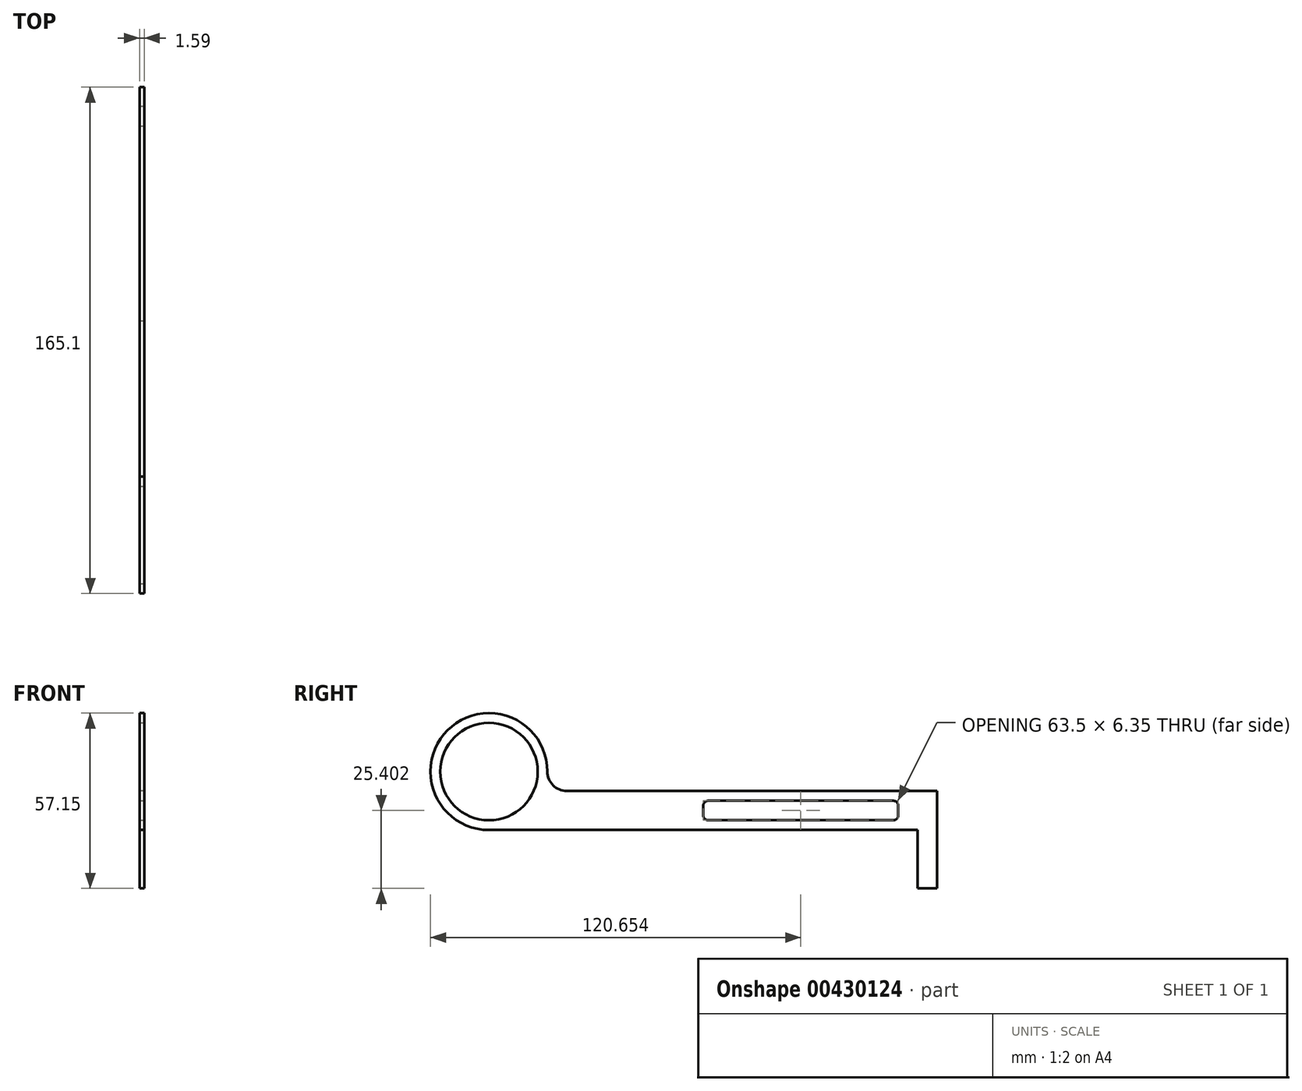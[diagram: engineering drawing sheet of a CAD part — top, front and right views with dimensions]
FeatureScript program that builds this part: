
annotation { "Feature Type Name" : "Feature", "Feature Type Description" : "" }
export const myFeature = defineFeature(function(context is Context, id is Id, definition is map)
    precondition{}
    {
        {
            var Q0;
            Q0=qCreatedBy(makeId("Right.planeOp"),FACE);
            var sketch = newSketch(context, id + "F0", { "sketchPlane" : qUnion([Q0])});
            skLineSegment(sketch, "E0", {"start": v(-101.24, 43.53) * mm, "end": v(-63.14, 43.53) * mm});
            skLineSegment(sketch, "E1", {"start": v(-63.14, 43.53) * mm, "end": v(-63.14, 18.13) * mm});
            skLineSegment(sketch, "E2", {"start": v(-63.14, 18.13) * mm, "end": v(63.86, 18.13) * mm});
            skLineSegment(sketch, "E3", {"start": v(63.86, 18.13) * mm, "end": v(63.86, -13.62) * mm});
            skLineSegment(sketch, "E4", {"start": v(63.86, -13.62) * mm, "end": v(57.51, -13.62) * mm});
            skLineSegment(sketch, "E5", {"start": v(57.51, -13.62) * mm, "end": v(57.51, 5.43) * mm});
            skLineSegment(sketch, "E6", {"start": v(57.51, 5.43) * mm, "end": v(-101.24, 5.43) * mm});
            skLineSegment(sketch, "E7", {"start": v(-101.24, 5.43) * mm, "end": v(-101.24, 43.53) * mm});
            skSolve(sketch);
        }
        {
            var Q0;
            Q0=qSketchRegion(id+"F0",true);
            extrude(context, id + "F1", {"entities" : qUnion([Q0]), "depth" : 1.59 * mm});
        }
        {
            var Q0;
            Q0=makeQuery(id+"F1.opExtrude","SWEPT_EDGE",EDGE,{"disambiguationData":[OSD([sQuery(id+"F0.wireOp",EDGE,"E0"),sQuery(id+"F0.wireOp",EDGE,"E1")])]});
            var Q1;
            Q1=makeQuery(id+"F1.opExtrude","SWEPT_EDGE",EDGE,{"disambiguationData":[OSD([sQuery(id+"F0.wireOp",EDGE,"E0"),sQuery(id+"F0.wireOp",EDGE,"E7")])]});
            var Q2;
            Q2=makeQuery(id+"F1.opExtrude","SWEPT_EDGE",EDGE,{"disambiguationData":[OSD([sQuery(id+"F0.wireOp",EDGE,"E6"),sQuery(id+"F0.wireOp",EDGE,"E7")])]});
            fillet(context, id + "F2", {"entities" : qUnion([Q0, Q1, Q2]), "radius" : 19.05 * mm, "tangentPropagation" : true, "allowEdgeOverflow" : false});
        }
        {
            var Q0;
            Q0=makeQuery(id+"F1.opExtrude","SWEPT_EDGE",EDGE,{"disambiguationData":[OSD([sQuery(id+"F0.wireOp",EDGE,"E1"),sQuery(id+"F0.wireOp",EDGE,"E2")])]});
            fillet(context, id + "F3", {"entities" : qUnion([Q0]), "radius" : 6.35 * mm, "tangentPropagation" : true, "allowEdgeOverflow" : false});
        }
        {
            var Q0;
            Q0=makeQuery(id+"F1.opExtrude","CAP_FACE",FACE,{"disambiguationData":[OSD([sQuery(id+"F0.wireOp",EDGE,"E0"),sQuery(id+"F0.wireOp",EDGE,"E1"),sQuery(id+"F0.wireOp",EDGE,"E2"),sQuery(id+"F0.wireOp",EDGE,"E3"),sQuery(id+"F0.wireOp",EDGE,"E4"),sQuery(id+"F0.wireOp",EDGE,"E5"),sQuery(id+"F0.wireOp",EDGE,"E6"),sQuery(id+"F0.wireOp",EDGE,"E7")])],"isStart":false});
            var sketch = newSketch(context, id + "F4", { "sketchPlane" : qUnion([Q0])});
            skCircle(sketch, "E8", {"center": v(-82.19, 24.48) * mm, "radius": 15.88 * mm});
            skSolve(sketch);
        }
        {
            var Q0;
            Q0=qSketchRegion(id+"F4",true);
            extrude(context, id + "F5", {"entities" : qUnion([Q0]), "operationType" : NewBodyOperationType.REMOVE, "oppositeDirection" : true, "depth" : 25.4 * mm});
        }
        {
            var Q0;
            Q0=makeQuery(id+"F1.opExtrude","CAP_FACE",FACE,{"disambiguationData":[OSD([sQuery(id+"F0.wireOp",EDGE,"E0"),sQuery(id+"F0.wireOp",EDGE,"E1"),sQuery(id+"F0.wireOp",EDGE,"E2"),sQuery(id+"F0.wireOp",EDGE,"E3"),sQuery(id+"F0.wireOp",EDGE,"E4"),sQuery(id+"F0.wireOp",EDGE,"E5"),sQuery(id+"F0.wireOp",EDGE,"E6"),sQuery(id+"F0.wireOp",EDGE,"E7")])],"isStart":false});
            var sketch = newSketch(context, id + "F6", { "sketchPlane" : qUnion([Q0])});
            skLineSegment(sketch, "E9.bottom", {"start": v(-12.34, 14.96) * mm, "end": v(51.16, 14.96) * mm});
            skLineSegment(sketch, "E9.top", {"start": v(-12.34, 8.6) * mm, "end": v(51.16, 8.6) * mm});
            skLineSegment(sketch, "E9.left", {"start": v(-12.34, 14.96) * mm, "end": v(-12.34, 8.6) * mm});
            skLineSegment(sketch, "E9.right", {"start": v(51.16, 14.96) * mm, "end": v(51.16, 8.6) * mm});
            skSolve(sketch);
        }
        {
            var Q0;
            Q0=qSketchRegion(id+"F6",true);
            extrude(context, id + "F7", {"entities" : qUnion([Q0]), "operationType" : NewBodyOperationType.REMOVE, "oppositeDirection" : true, "depth" : 25.4 * mm});
        }
        {
            var Q0;
            Q0=makeQuery(id+"F7.boolean.opBoolean","COPY",EDGE,{"derivedFrom":makeQuery(id+"F7.opExtrude","SWEPT_EDGE",EDGE,{"disambiguationData":[OSD([sQuery(id+"F6.wireOp",EDGE,"E9.bottom"),sQuery(id+"F6.wireOp",EDGE,"E9.left")])]})});
            var Q1;
            Q1=makeQuery(id+"F7.boolean.opBoolean","COPY",EDGE,{"derivedFrom":makeQuery(id+"F7.opExtrude","SWEPT_EDGE",EDGE,{"disambiguationData":[OSD([sQuery(id+"F6.wireOp",EDGE,"E9.top"),sQuery(id+"F6.wireOp",EDGE,"E9.left")])]})});
            var Q2;
            Q2=makeQuery(id+"F7.boolean.opBoolean","COPY",EDGE,{"derivedFrom":makeQuery(id+"F7.opExtrude","SWEPT_EDGE",EDGE,{"disambiguationData":[OSD([sQuery(id+"F6.wireOp",EDGE,"E9.top"),sQuery(id+"F6.wireOp",EDGE,"E9.right")])]})});
            var Q3;
            Q3=makeQuery(id+"F7.boolean.opBoolean","COPY",EDGE,{"derivedFrom":makeQuery(id+"F7.opExtrude","SWEPT_EDGE",EDGE,{"disambiguationData":[OSD([sQuery(id+"F6.wireOp",EDGE,"E9.bottom"),sQuery(id+"F6.wireOp",EDGE,"E9.right")])]})});
            fillet(context, id + "F8", {"entities" : qUnion([Q0, Q1, Q2, Q3]), "radius" : 1.59 * mm, "tangentPropagation" : true, "allowEdgeOverflow" : false});
        }
    });
